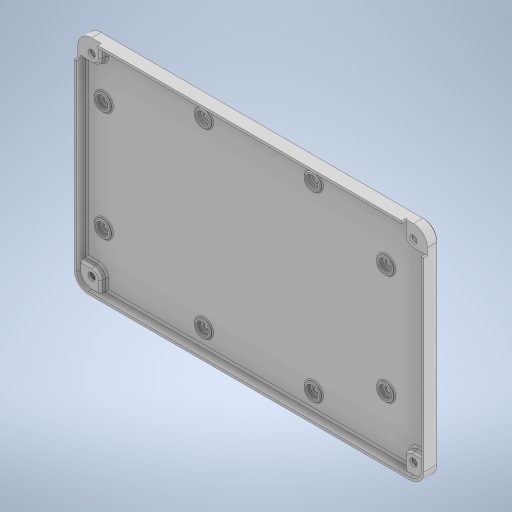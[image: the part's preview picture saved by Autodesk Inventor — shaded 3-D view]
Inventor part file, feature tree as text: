
AUTODESK INVENTOR PART (.ipt)
format: ipt  version: 2023.1 (Build 271208000, 208)  size: 951,808 bytes
history: native  units: mm
features: projected_geometry x16, sketch x13, extrude x12, chamfer x8, reference x8, move_body x6, direct_edit x5, other x5, hole x2, delete_face x2
ambient origin geometry x8: Origin, YZ Plane, XZ Plane, XY Plane, X Axis, Y Axis, Z Axis, Center Point
bodies: Volumenkörper1 (feature_tree)
feature tree (77):
  extrude  "Extrusion1"  Depth=90.0mm
  extrude  "Extrusion2"  Depth=162.989398mm
  extrude  "Extrusion3"  Depth=100.6mm
  extrude  "Extrusion4"  Depth=1.2mm
  hole  "Bohrung1"  [1 undecoded]
  extrude  "Extrusion5"  Depth=1.2mm
  hole  "Bohrung2"  [1 undecoded]
  extrude  "Extrusion6"  Depth=8.0mm
  chamfer  "Fase1"  Distance=5.0mm
  extrude  "Extrusion7"  Depth=2.0mm TaperAngle=0.0deg
  chamfer  "Fase2"  Distance=85.0mm
  chamfer  "Fase3"  Distance=42.5mm
  chamfer  "Fase4"  Distance=9.0mm
  chamfer  "Fase5"  Distance=9.0mm
  chamfer  "Fase6"  Distance=9.0mm
  extrude  "Extrusion8"  Depth=10.0mm
  extrude  "Extrusion9"  Depth=10.0mm
  delete_face  "Fläche löschen1"
  sketch  "Skizze12"  dims[d24=0.6mm d25=0.0mm d26=2.0mm d27=0.0mm]
  extrude  "Extrusion10"  Depth=10.0mm
  extrude  "Extrusion11"  Depth=10.0mm TaperAngle=0.0deg
  extrude  "Extrusion12"  Depth=10.0mm TaperAngle=0.0deg
  chamfer  "Fase7"  Distance=0.4mm Angle=45.0deg
  direct_edit  "Direktbearbeitung1"
  direct_edit  "Direktbearbeitung2"
  direct_edit  "Direktbearbeitung3"
  direct_edit  "Direktbearbeitung4"
  direct_edit  "Direktbearbeitung5"
  delete_face  "Fläche löschen2"
  chamfer  "Fase8"  Distance=0.3mm
  sketch  "Skizze1"  dims[d0=150.0mm d1=90.0mm]
  reference  "Referenz1"
  reference  "Referenz2"
  reference  "Referenz3"
  reference  "Referenz4"
  reference  "Referenz5"
  reference  "Referenz6"
  sketch  "Skizze2"  dims[d4=103.000003mm d5=162.989398mm]
  projected_geometry  "Projizierte Kontur1"
  sketch  "Skizze3"  dims[d6=163.6mm d7=100.6mm]
  projected_geometry  "Projizierte Kontur2"
  sketch  "Skizze4"  dims[d8=4.999998mm d9=1.2mm]
  projected_geometry  "Projizierte Kontur3"
  sketch  "Skizze5"  dims[d10=1.2mm d11=160.6mm]
  projected_geometry  "Projizierte Kontur4"
  sketch  "Skizze6"  dims[d12=100.6mm d13=1.2mm]
  sketch  "Skizze7"  dims[d14=1.2mm d15=1.2mm]
  projected_geometry  "Projizierte Kontur5"
  sketch  "Skizze8"  dims[d16=1.6mm d17=0.0mm d18=8.0mm]
  projected_geometry  "Projizierte Kontur6"
  sketch  "Skizze9"  dims[d19=8.0mm]
  reference  "Referenz7"
  reference  "Referenz8"
  projected_geometry  "Projizierte Kontur7"
  sketch  "Skizze10"  dims[d20=8.0mm]
  projected_geometry  "Projizierte Kontur8"
  projected_geometry  "Projizierte Kontur9"
  projected_geometry  "Projizierte Kontur10"
  projected_geometry  "Projizierte Kontur11"
  sketch  "Skizze11"  dims[d21=8.0mm d22=5.0mm d23=0.0mm]
  sketch  "Skizze13"  dims[d28=3.34mm d29=6.0mm d30=5.8mm d31=4.6mm d32=90.0deg d33=8.0mm d34=20.594885mm d35=51.3mm d36=5.6mm d37=1.2mm d38=5.6mm d39=1.2mm d42=8.0mm d43=8.0mm d44=8.0mm d46=132.0mm d47=51.3mm d52=8.0mm d53=8.0mm d54=8.0mm d55=8.0mm d56=85.0mm d57=42.5mm d59=9.0mm d60=9.0mm d61=9.0mm d62=22.0mm d63=163.0mm d64=81.5mm d65=1.0mm d66=0.0mm d67=3.34mm d68=6.0mm d69=5.8mm d70=2.2mm d71=90.0deg d72=8.0mm d73=20.594885mm d74=0.8mm d75=0.0mm d76=0.4mm d77=2.0mm d78=45.0deg d79=0.3mm d80=0.3mm d81=0.3mm d82=0.3mm d83=0.8mm d84=0.0mm d85=0.8mm d86=2.0mm d87=45.0deg d88=1.0mm d89=2.0mm d90=45.0deg d91=0.8mm d92=2.0mm d93=45.0deg d94=0.4mm d95=2.0mm d96=45.0deg d97=0.4mm d98=2.0mm d99=45.0deg d100=0.2mm d101=0.0mm d102=0.4mm d103=0.0mm d104=5.6mm d105=5.6mm d106=10.0mm d107=0.0mm d108=10.0mm d109=0.0mm d110=10.0mm d111=0.0mm d112=0.4mm d113=2.0mm d114=45.0deg d115=-0.2mm d116=0.0mm d117=0.0mm d118=0.2mm d119=0.0mm d120=0.0mm d121=0.0mm d122=-0.1mm d123=0.0mm d124=0.0mm d125=0.1mm d126=0.0mm d127=-0.2mm d128=0.0mm d129=0.0mm d130=0.0mm d131=0.0mm d132=-0.2mm d133=0.4mm d134=2.0mm d135=45.0deg]
  projected_geometry  "Projizierte Kontur12"
  projected_geometry  "Projizierte Kontur13"
  projected_geometry  "Projizierte Kontur14"
  projected_geometry  "Projizierte Kontur15"
  projected_geometry  "Projizierte Kontur16"
  other  "<userpath>\Desktop\GitHub\Voron-2-Mods\Mix\Octopus_Pro_FanCase\CAD\FanCase_Assembly.iam"
  other  "FanCase_Assembly.iam"
  other  "Buttom:1"
  other  "Octopus2:1"
  other  "FanCase_Middle:1"
  move_body  "Verschieben1"
  move_body  "Verschieben2"
  move_body  "Verschieben3"
  move_body  "Verschieben4"
  move_body  "Verschieben5"
  move_body  "Verschieben6"
note: 2 required parameter values undecoded (feature->parameter linkage not recoverable at this tier; creation-order binding heuristic only, values carry confidence <= 0.55)
